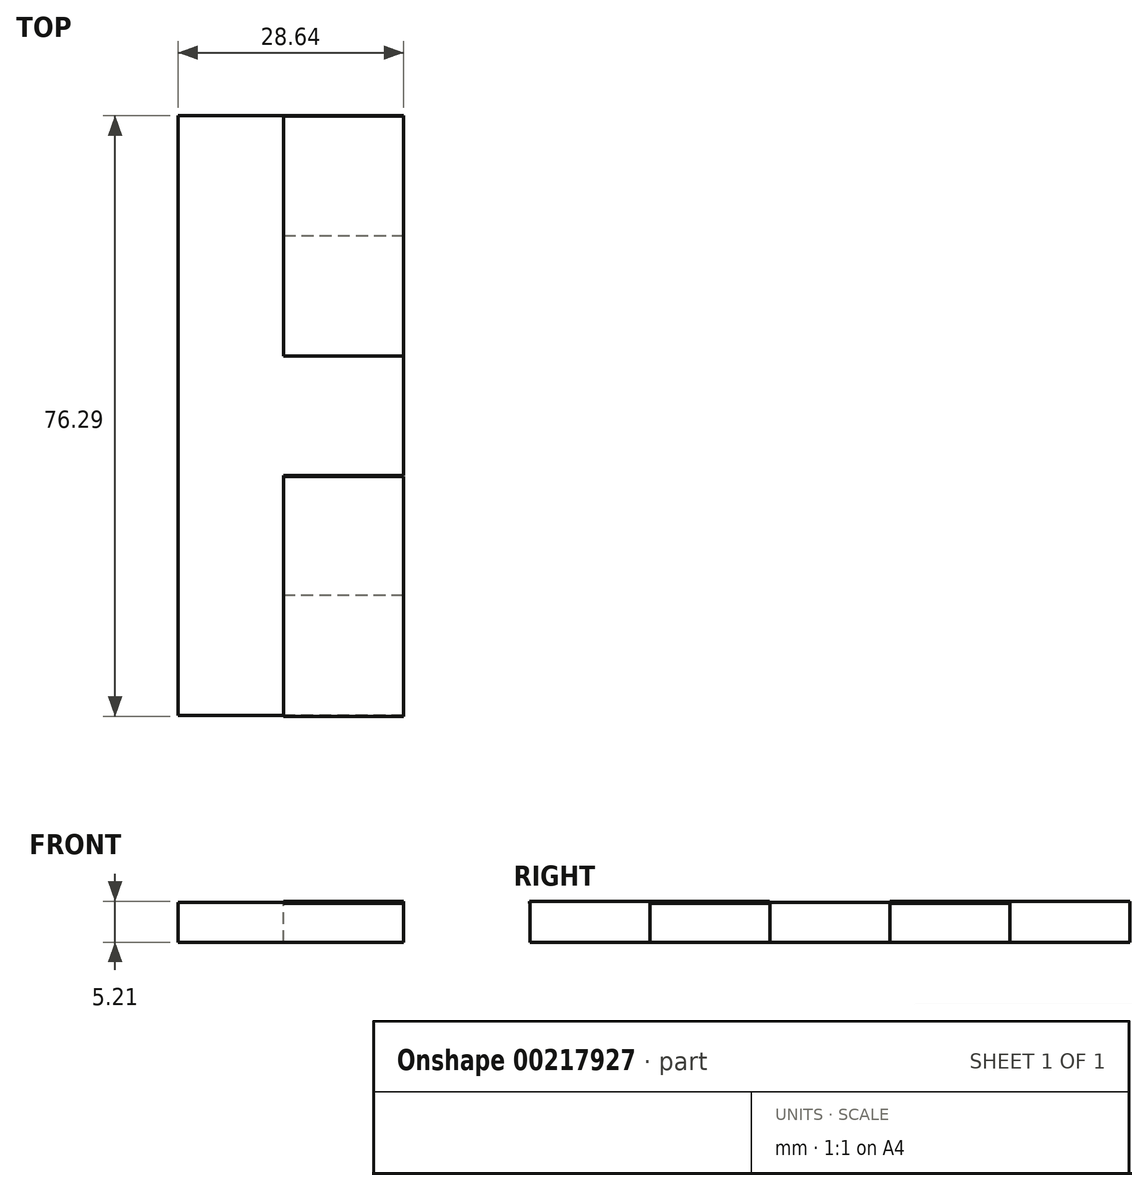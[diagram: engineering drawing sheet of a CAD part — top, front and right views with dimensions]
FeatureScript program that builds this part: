
annotation { "Feature Type Name" : "Feature", "Feature Type Description" : "" }
export const myFeature = defineFeature(function(context is Context, id is Id, definition is map)
    precondition{}
    {
        {
            var Q0;
            Q0=qCreatedBy(makeId("Top.planeOp"),FACE);
            var sketch = newSketch(context, id + "F0", { "sketchPlane" : qUnion([Q0])});
            skLineSegment(sketch, "E0", {"start": v(-28.64, 45.81) * mm, "end": v(0, 45.81) * mm});
            skLineSegment(sketch, "E1", {"start": v(0, 45.81) * mm, "end": v(0, 30.57) * mm});
            skLineSegment(sketch, "E2", {"start": v(0, 30.57) * mm, "end": v(-15.24, 30.57) * mm});
            skLineSegment(sketch, "E3", {"start": v(-15.24, 30.57) * mm, "end": v(-15.24, 15.33) * mm});
            skLineSegment(sketch, "E4", {"start": v(-15.24, 15.33) * mm, "end": v(0, 15.33) * mm});
            skLineSegment(sketch, "E5", {"start": v(0, 15.33) * mm, "end": v(0, 0.1) * mm});
            skLineSegment(sketch, "E6", {"start": v(0, 0.1) * mm, "end": v(-15.24, 0.1) * mm});
            skLineSegment(sketch, "E7", {"start": v(-15.24, 0.1) * mm, "end": v(-15.24, -15.15) * mm});
            skLineSegment(sketch, "E8", {"start": v(-15.24, -15.15) * mm, "end": v(0, -15.15) * mm});
            skLineSegment(sketch, "E9", {"start": v(0, -15.15) * mm, "end": v(0, -30.39) * mm});
            skLineSegment(sketch, "E10", {"start": v(-28.64, 45.81) * mm, "end": v(-28.64, -30.39) * mm});
            skLineSegment(sketch, "E11", {"start": v(-28.64, -30.39) * mm, "end": v(0, -30.39) * mm});
            skSolve(sketch);
        }
        {
            var Q0;
            Q0=qSketchRegion(id+"F0",true);
            extrude(context, id + "F1", {"entities" : qUnion([Q0]), "oppositeDirection" : true, "depth" : 5.08 * mm});
        }
        {
            var Q0;
            Q0=qCreatedBy(makeId("Top.planeOp"),FACE);
            var sketch = newSketch(context, id + "F2", { "sketchPlane" : qUnion([Q0])});
            skLineSegment(sketch, "E12", {"start": v(0, 45.77) * mm, "end": v(-15.24, 45.77) * mm});
            skLineSegment(sketch, "E13", {"start": v(-15.24, 45.77) * mm, "end": v(-15.24, 15.3) * mm});
            skLineSegment(sketch, "E14", {"start": v(-15.24, 15.3) * mm, "end": v(0, 15.3) * mm});
            skLineSegment(sketch, "E15", {"start": v(0, 15.3) * mm, "end": v(0, 45.77) * mm});
            skLineSegment(sketch, "E16", {"start": v(0, 0) * mm, "end": v(-15.24, 0) * mm});
            skLineSegment(sketch, "E17", {"start": v(-15.24, 0) * mm, "end": v(-15.24, -30.48) * mm});
            skLineSegment(sketch, "E18", {"start": v(-15.24, -30.48) * mm, "end": v(0, -30.48) * mm});
            skLineSegment(sketch, "E19", {"start": v(0, -30.48) * mm, "end": v(0, 0) * mm});
            skSolve(sketch);
        }
        {
            var Q0;
            Q0 = qSketchRegion(id + "F2", true);
            extrude(context, id + "F3", {"entities" : qUnion([Q0]), "operationType" : NewBodyOperationType.ADD, "endBound" : BoundingType.SYMMETRIC, "oppositeDirection" : true, "depth" : 0.25 * mm});
        }
    });
